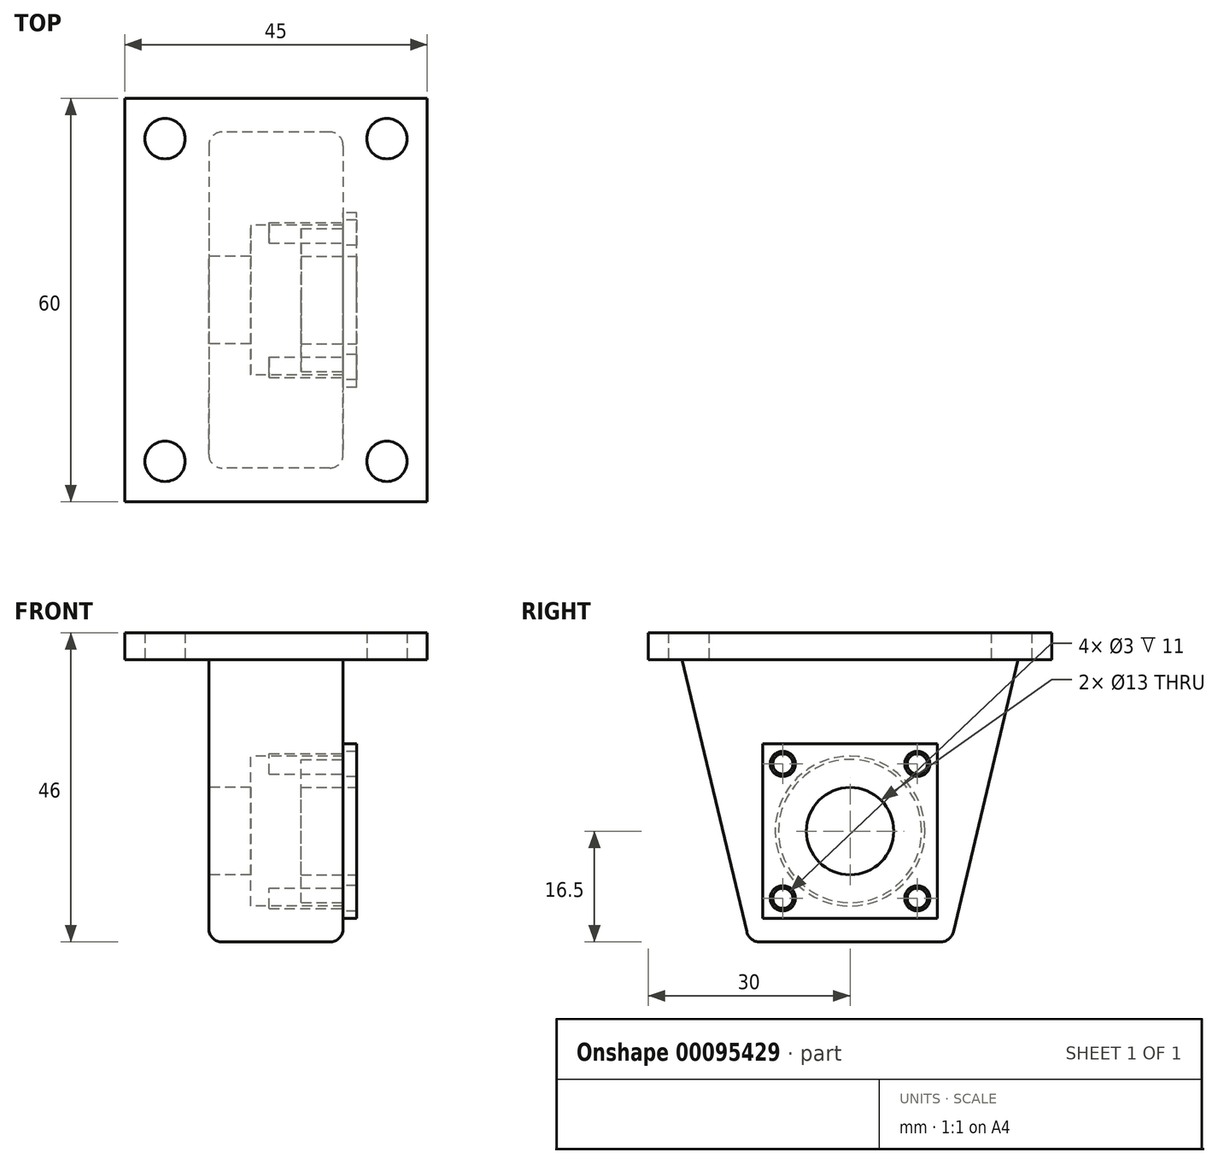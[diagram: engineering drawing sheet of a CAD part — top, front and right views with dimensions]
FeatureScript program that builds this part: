
annotation { "Feature Type Name" : "Feature", "Feature Type Description" : "" }
export const myFeature = defineFeature(function(context is Context, id is Id, definition is map)
    precondition{}
    {
        {
            var Q0;
            Q0=qCreatedBy(makeId("Top.planeOp"),FACE);
            var sketch = newSketch(context, id + "F0", { "sketchPlane" : qUnion([Q0])});
            skLineSegment(sketch, "E0.bottom", {"start": v(22.5, 30) * mm, "end": v(-22.5, 30) * mm});
            skLineSegment(sketch, "E0.top", {"start": v(22.5, -30) * mm, "end": v(-22.5, -30) * mm});
            skLineSegment(sketch, "E0.left", {"start": v(22.5, 30) * mm, "end": v(22.5, -30) * mm});
            skLineSegment(sketch, "E0.right", {"start": v(-22.5, 30) * mm, "end": v(-22.5, -30) * mm});
            skPoint(sketch, "E0.middle", {"position": v(0, 0) * mm});
            skCircle(sketch, "E1", {"center": v(-16.5, 24) * mm, "radius": 3 * mm});
            skCircle(sketch, "E2", {"center": v(-16.5, -24) * mm, "radius": 3 * mm});
            skCircle(sketch, "E3", {"center": v(16.5, 24) * mm, "radius": 3 * mm});
            skCircle(sketch, "E4", {"center": v(16.5, -24) * mm, "radius": 3 * mm});
            skSolve(sketch);
        }
        {
            var Q0;
            Q0=makeQuery(id+"F0.imprint","IMPRINT",FACE,{"disambiguationData":[TD([[makeQuery(id+"F0.imprint","IMPRINT",EDGE,{"derivedFrom":sQuery(id+"F0.wireOp",EDGE,"E0.bottom")}),1.0]])]});
            extrude(context, id + "F1", {"entities" : qUnion([Q0]), "depth" : 4 * mm});
        }
        {
            var Q0;
            Q0=qCreatedBy(makeId("Right.planeOp"),FACE);
            var sketch = newSketch(context, id + "F2", { "sketchPlane" : qUnion([Q0])});
            skLineSegment(sketch, "E5.bottom", {"start": v(25, 0) * mm, "end": v(-25, 0) * mm});
            skLineSegment(sketch, "E5.top", {"start": v(25, -42) * mm, "end": v(-25, -42) * mm});
            skLineSegment(sketch, "E5.left", {"start": v(25, 0) * mm, "end": v(25, -42) * mm});
            skLineSegment(sketch, "E5.right", {"start": v(-25, 0) * mm, "end": v(-25, -42) * mm});
            skLineSegment(sketch, "E6", {"start": v(25, 0) * mm, "end": v(15, -42) * mm});
            skLineSegment(sketch, "E7", {"start": v(-25, 0) * mm, "end": v(-15, -42) * mm});
            skCircle(sketch, "E8", {"center": v(0, -25.5) * mm, "radius": 11.15 * mm});
            skSolve(sketch);
        }
        {
            var Q0;
            Q0=makeQuery(id+"F2.imprint","IMPRINT",FACE,{"disambiguationData":[TD([[makeQuery(id+"F2.imprint","IMPRINT",EDGE,{"derivedFrom":sQuery(id+"F2.wireOp",EDGE,"E5.bottom")}),1.0]])]});
            extrude(context, id + "F3", {"entities" : qUnion([Q0]), "operationType" : NewBodyOperationType.ADD, "endBound" : BoundingType.SYMMETRIC, "depth" : 20 * mm});
        }
        {
            var Q0;
            Q0=makeQuery(id+"F3.opExtrude","CAP_FACE",FACE,{"disambiguationData":[OSD([sQuery(id+"F2.wireOp",EDGE,"E5.bottom"),sQuery(id+"F2.wireOp",EDGE,"E5.top"),sQuery(id+"F2.wireOp",EDGE,"E6"),sQuery(id+"F2.wireOp",EDGE,"E7"),sQuery(id+"F2.wireOp",EDGE,"E8")])],"isStart":true});
            var sketch = newSketch(context, id + "F4", { "sketchPlane" : qUnion([Q0])});
            skCircle(sketch, "E9", {"center": v(0, -25.5) * mm, "radius": 11.15 * mm});
            skCircle(sketch, "E10", {"center": v(0, -25.5) * mm, "radius": 6.5 * mm});
            skSolve(sketch);
        }
        {
            var Q0;
            Q0=makeQuery(id+"F4.imprint","IMPRINT",FACE,{"disambiguationData":[TD([[makeQuery(id+"F4.imprint","IMPRINT",EDGE,{"derivedFrom":sQuery(id+"F4.wireOp",EDGE,"E9")}),-1.0]])]});
            extrude(context, id + "F5", {"entities" : qUnion([Q0]), "operationType" : NewBodyOperationType.ADD, "oppositeDirection" : true, "depth" : 6.25 * mm});
        }
        {
            var Q0;
            Q0=makeQuery(id+"F3.opExtrude","CAP_FACE",FACE,{"disambiguationData":[OSD([sQuery(id+"F2.wireOp",EDGE,"E5.bottom"),sQuery(id+"F2.wireOp",EDGE,"E5.top"),sQuery(id+"F2.wireOp",EDGE,"E6"),sQuery(id+"F2.wireOp",EDGE,"E7"),sQuery(id+"F2.wireOp",EDGE,"E8")])],"isStart":false});
            var sketch = newSketch(context, id + "F6", { "sketchPlane" : qUnion([Q0])});
            skCircle(sketch, "E11", {"center": v(0, -25.5) * mm, "radius": 10.65 * mm});
            skCircle(sketch, "E12", {"center": v(0, -25.5) * mm, "radius": 6.5 * mm});
            skLineSegment(sketch, "E13.bottom", {"start": v(-13, -12.5) * mm, "end": v(13, -12.5) * mm});
            skLineSegment(sketch, "E13.top", {"start": v(-13, -38.5) * mm, "end": v(13, -38.5) * mm});
            skLineSegment(sketch, "E13.left", {"start": v(-13, -12.5) * mm, "end": v(-13, -38.5) * mm});
            skLineSegment(sketch, "E13.right", {"start": v(13, -12.5) * mm, "end": v(13, -38.5) * mm});
            skCircle(sketch, "E14", {"center": v(-10, -15.5) * mm, "radius": 1.88 * mm});
            skCircle(sketch, "E15", {"center": v(10, -15.5) * mm, "radius": 1.88 * mm});
            skCircle(sketch, "E16", {"center": v(-10, -35.5) * mm, "radius": 1.88 * mm});
            skCircle(sketch, "E17", {"center": v(10, -35.5) * mm, "radius": 1.88 * mm});
            skSolve(sketch);
        }
        {
            var Q0;
            Q0=makeQuery(id+"F6.imprint","IMPRINT",FACE,{"disambiguationData":[TD([[makeQuery(id+"F6.imprint","IMPRINT",EDGE,{"derivedFrom":sQuery(id+"F6.wireOp",EDGE,"E11")}),1.0]])]});
            extrude(context, id + "F7", {"entities" : qUnion([Q0]), "oppositeDirection" : true, "depth" : 6.25 * mm});
        }
        {
            var Q0;
            Q0=makeQuery(id+"F6.imprint","IMPRINT",FACE,{"disambiguationData":[TD([[makeQuery(id+"F6.imprint","IMPRINT",EDGE,{"derivedFrom":sQuery(id+"F6.wireOp",EDGE,"E13.bottom")}),-1.0]])]});
            var Q1;
            Q1=makeQuery(id+"F6.imprint","IMPRINT",FACE,{"disambiguationData":[TD([[makeQuery(id+"F6.imprint","IMPRINT",EDGE,{"derivedFrom":sQuery(id+"F6.wireOp",EDGE,"E11")}),-1.0]])]});
            var Q2;
            Q2=makeQuery(id+"F6.imprint","IMPRINT",FACE,{"disambiguationData":[TD([[makeQuery(id+"F6.imprint","IMPRINT",EDGE,{"derivedFrom":sQuery(id+"F6.wireOp",EDGE,"E11")}),1.0]])]});
            extrude(context, id + "F8", {"entities" : qUnion([Q0, Q1, Q2]), "operationType" : NewBodyOperationType.ADD, "depth" : 2 * mm});
        }
        {
            var Q0;
            Q0=makeQuery(id+"F6.imprint","IMPRINT",FACE,{"disambiguationData":[TD([[makeQuery(id+"F6.imprint","IMPRINT",EDGE,{"derivedFrom":sQuery(id+"F6.wireOp",EDGE,"E13.bottom")}),1.0]])]});
            var sketch = newSketch(context, id + "F9", { "sketchPlane" : qUnion([Q0])});
            skCircle(sketch, "E18", {"center": v(-10, -15.5) * mm, "radius": 1.5 * mm});
            skCircle(sketch, "E19", {"center": v(10, -15.5) * mm, "radius": 1.5 * mm});
            skCircle(sketch, "E20", {"center": v(10, -35.5) * mm, "radius": 1.5 * mm});
            skCircle(sketch, "E21", {"center": v(-10, -35.5) * mm, "radius": 1.5 * mm});
            skSolve(sketch);
        }
        {
            var Q0;
            Q0=makeQuery(id+"F9.imprint","IMPRINT",FACE,{"disambiguationData":[TD([[makeQuery(id+"F9.imprint","IMPRINT",EDGE,{"derivedFrom":sQuery(id+"F9.wireOp",EDGE,"E18")}),1.0]])]});
            var Q1;
            Q1=makeQuery(id+"F9.imprint","IMPRINT",FACE,{"disambiguationData":[TD([[makeQuery(id+"F9.imprint","IMPRINT",EDGE,{"derivedFrom":sQuery(id+"F9.wireOp",EDGE,"E19")}),1.0]])]});
            var Q2;
            Q2=makeQuery(id+"F9.imprint","IMPRINT",FACE,{"disambiguationData":[TD([[makeQuery(id+"F9.imprint","IMPRINT",EDGE,{"derivedFrom":sQuery(id+"F9.wireOp",EDGE,"E20")}),1.0]])]});
            var Q3;
            Q3=makeQuery(id+"F9.imprint","IMPRINT",FACE,{"disambiguationData":[TD([[makeQuery(id+"F9.imprint","IMPRINT",EDGE,{"derivedFrom":sQuery(id+"F9.wireOp",EDGE,"E21")}),1.0]])]});
            extrude(context, id + "F10", {"entities" : qUnion([Q0, Q1, Q2, Q3]), "operationType" : NewBodyOperationType.REMOVE, "oppositeDirection" : true, "depth" : 11 * mm});
        }
        {
            var Q0;
            Q0=makeQuery(id+"F3.opExtrude","CAP_EDGE",EDGE,{"disambiguationData":[OSD([sQuery(id+"F2.wireOp",EDGE,"E5.top")])],"isStart":false});
            var Q1;
            Q1=makeQuery(id+"F3.opExtrude","SWEPT_EDGE",EDGE,{"disambiguationData":[OSD([sQuery(id+"F2.wireOp",EDGE,"E5.top"),sQuery(id+"F2.wireOp",EDGE,"E6")])]});
            var Q2;
            Q2=makeQuery(id+"F3.opExtrude","CAP_EDGE",EDGE,{"disambiguationData":[OSD([sQuery(id+"F2.wireOp",EDGE,"E5.top")])],"isStart":true});
            var Q3;
            Q3=makeQuery(id+"F3.opExtrude","SWEPT_EDGE",EDGE,{"disambiguationData":[OSD([sQuery(id+"F2.wireOp",EDGE,"E5.top"),sQuery(id+"F2.wireOp",EDGE,"E7")])]});
            var Q4;
            Q4=makeQuery(id+"F3.opExtrude","CAP_EDGE",EDGE,{"disambiguationData":[OSD([sQuery(id+"F2.wireOp",EDGE,"E6")])],"isStart":false});
            var Q5;
            Q5=makeQuery(id+"F3.opExtrude","CAP_EDGE",EDGE,{"disambiguationData":[OSD([sQuery(id+"F2.wireOp",EDGE,"E6")])],"isStart":true});
            var Q6;
            Q6=makeQuery(id+"F3.opExtrude","CAP_EDGE",EDGE,{"disambiguationData":[OSD([sQuery(id+"F2.wireOp",EDGE,"E7")])],"isStart":false});
            var Q7;
            Q7=makeQuery(id+"F3.opExtrude","CAP_EDGE",EDGE,{"disambiguationData":[OSD([sQuery(id+"F2.wireOp",EDGE,"E7")])],"isStart":true});
            fillet(context, id + "F11", {"entities" : qUnion([Q0, Q1, Q2, Q3, Q4, Q5, Q6, Q7]), "radius" : 2 * mm, "tangentPropagation" : true, "allowEdgeOverflow" : false});
        }
    });
